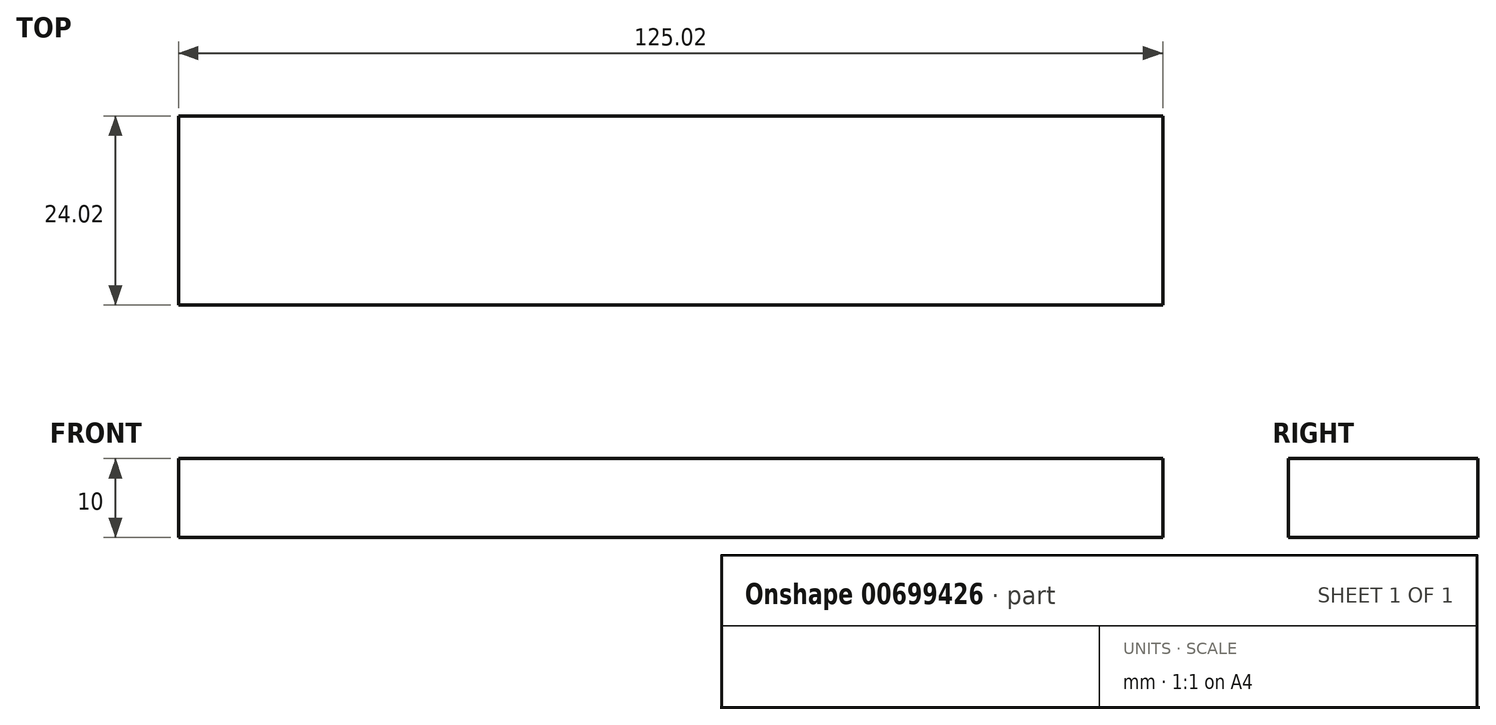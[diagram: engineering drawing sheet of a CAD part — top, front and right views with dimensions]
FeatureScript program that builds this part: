
annotation { "Feature Type Name" : "Feature", "Feature Type Description" : "" }
export const myFeature = defineFeature(function(context is Context, id is Id, definition is map)
    precondition{}
    {
        {
            var Q0;
            Q0=qCreatedBy(makeId("Top.planeOp"),FACE);
            var sketch = newSketch(context, id + "F0", { "sketchPlane" : qUnion([Q0])});
            skLineSegment(sketch, "E0.bottom", {"start": v(0, 0) * mm, "end": v(125.02, 0) * mm});
            skLineSegment(sketch, "E0.top", {"start": v(0, -24.02) * mm, "end": v(125.02, -24.02) * mm});
            skLineSegment(sketch, "E0.left", {"start": v(0, 0) * mm, "end": v(0, -24.02) * mm});
            skLineSegment(sketch, "E0.right", {"start": v(125.02, 0) * mm, "end": v(125.02, -24.02) * mm});
            skSolve(sketch);
        }
        {
            var Q0;
            Q0=makeQuery(id+"F0.imprint","IMPRINT",FACE,{"disambiguationData":[TD([[makeQuery(id+"F0.imprint","IMPRINT",EDGE,{"derivedFrom":sQuery(id+"F0.wireOp",EDGE,"E0.bottom")}),-1.0]])]});
            extrude(context, id + "F1", {"entities" : qUnion([Q0]), "depth" : 10 * mm, "offsetDistance" : 25 * mm});
        }
    });
